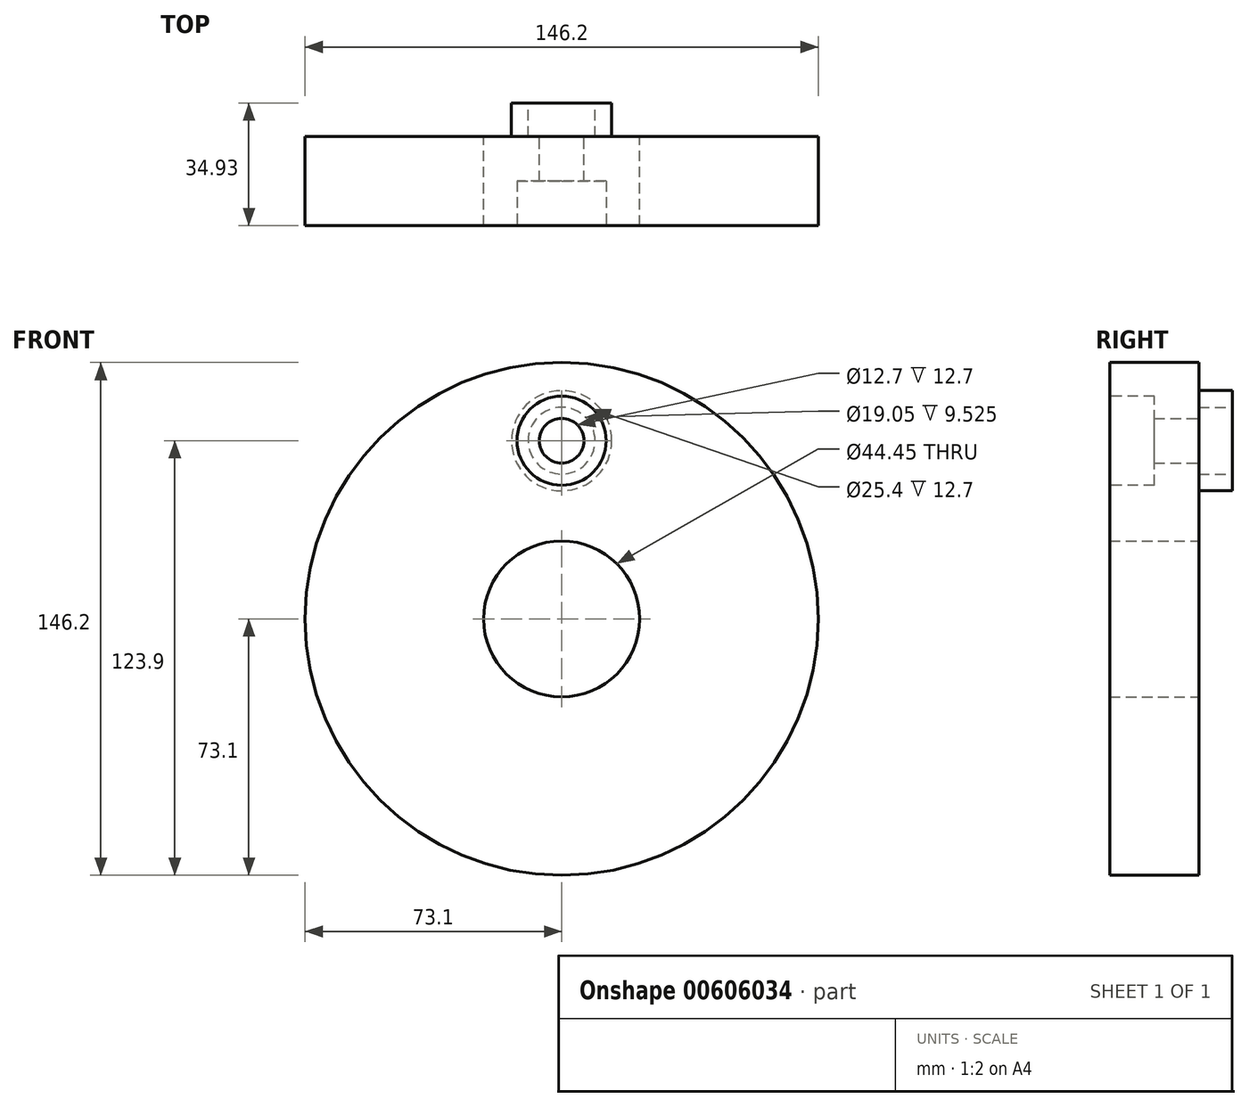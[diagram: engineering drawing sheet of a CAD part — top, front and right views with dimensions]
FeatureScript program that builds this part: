
annotation { "Feature Type Name" : "Feature", "Feature Type Description" : "" }
export const myFeature = defineFeature(function(context is Context, id is Id, definition is map)
    precondition{}
    {
        {
            var Q0;
            Q0=qCreatedBy(makeId("Front.planeOp"),FACE);
            var sketch = newSketch(context, id + "F0", { "sketchPlane" : qUnion([Q0])});
            skCircle(sketch, "E0", {"center": v(0, 0) * mm, "radius": 73.1 * mm});
            skSolve(sketch);
        }
        {
            var Q0;
            Q0=makeQuery(id+"F0.imprint","IMPRINT",FACE,{"disambiguationData":[TD([[makeQuery(id+"F0.imprint","IMPRINT",EDGE,{"derivedFrom":sQuery(id+"F0.wireOp",EDGE,"E0")}),1.0]])]});
            extrude(context, id + "F1", {"entities" : qUnion([Q0]), "depth" : 25.4 * mm, "offsetDistance" : 25.4 * mm});
        }
        {
            var Q0;
            Q0=makeQuery(id+"F1.opExtrude","CAP_FACE",FACE,{"disambiguationData":[OSD([sQuery(id+"F0.wireOp",EDGE,"E0")])],"isStart":true});
            var sketch = newSketch(context, id + "F2", { "sketchPlane" : qUnion([Q0])});
            skCircle(sketch, "E1", {"center": v(0, 50.8) * mm, "radius": 6.35 * mm});
            skSolve(sketch);
        }
        {
            var Q0;
            Q0 = qSketchRegion(id + "F2", true);
            extrude(context, id + "F3", {"entities" : qUnion([Q0]), "operationType" : NewBodyOperationType.REMOVE, "oppositeDirection" : true, "depth" : 25.4 * mm, "offsetDistance" : 25.4 * mm});
        }
        {
            var Q0;
            Q0=makeQuery(id+"F1.opExtrude","CAP_FACE",FACE,{"disambiguationData":[OSD([sQuery(id+"F0.wireOp",EDGE,"E0")])],"isStart":true});
            var sketch = newSketch(context, id + "F4", { "sketchPlane" : qUnion([Q0])});
            skCircle(sketch, "E2", {"center": v(0, 50.8) * mm, "radius": 14.29 * mm});
            skSolve(sketch);
        }
        {
            var Q0;
            Q0=makeQuery(id+"F4.imprint","IMPRINT",FACE,{"disambiguationData":[TD([[makeQuery(id+"F4.imprint","IMPRINT",EDGE,{"derivedFrom":sQuery(id+"F4.wireOp",EDGE,"E2")}),1.0]])]});
            extrude(context, id + "F5", {"entities" : qUnion([Q0]), "operationType" : NewBodyOperationType.ADD, "depth" : 9.52 * mm, "offsetDistance" : 25.4 * mm});
        }
        {
            var Q0;
            Q0=makeQuery(id+"F5.opExtrude","CAP_FACE",FACE,{"disambiguationData":[OSD([sQuery(id+"F2.wireOp",EDGE,"E1"),sQuery(id+"F4.wireOp",EDGE,"E2")])],"isStart":false});
            var sketch = newSketch(context, id + "F6", { "sketchPlane" : qUnion([Q0])});
            skCircle(sketch, "E3", {"center": v(0, 50.8) * mm, "radius": 9.53 * mm});
            skSolve(sketch);
        }
        {
            var Q0;
            Q0 = qSketchRegion(id + "F6", true);
            extrude(context, id + "F7", {"entities" : qUnion([Q0]), "operationType" : NewBodyOperationType.REMOVE, "oppositeDirection" : true, "depth" : 9.52 * mm, "offsetDistance" : 25.4 * mm});
        }
        {
            var Q0;
            Q0=makeQuery(id+"F1.opExtrude","CAP_FACE",FACE,{"disambiguationData":[OSD([sQuery(id+"F0.wireOp",EDGE,"E0")])],"isStart":true});
            var sketch = newSketch(context, id + "F8", { "sketchPlane" : qUnion([Q0])});
            skCircle(sketch, "E4", {"center": v(0, 0) * mm, "radius": 22.23 * mm});
            skSolve(sketch);
        }
        {
            var Q0;
            Q0 = qSketchRegion(id + "F8", true);
            extrude(context, id + "F9", {"entities" : qUnion([Q0]), "operationType" : NewBodyOperationType.REMOVE, "oppositeDirection" : true, "depth" : 25.4 * mm, "offsetDistance" : 25.4 * mm});
        }
        {
            var Q0;
            Q0=makeQuery(id+"F1.opExtrude","CAP_FACE",FACE,{"disambiguationData":[OSD([sQuery(id+"F0.wireOp",EDGE,"E0")])],"isStart":false});
            var sketch = newSketch(context, id + "F10", { "sketchPlane" : qUnion([Q0])});
            skCircle(sketch, "E5", {"center": v(0, 50.8) * mm, "radius": 12.7 * mm});
            skSolve(sketch);
        }
        {
            var Q0;
            Q0 = qSketchRegion(id + "F10", true);
            extrude(context, id + "F11", {"entities" : qUnion([Q0]), "operationType" : NewBodyOperationType.REMOVE, "oppositeDirection" : true, "depth" : 12.7 * mm, "offsetDistance" : 25.4 * mm});
        }
    });
